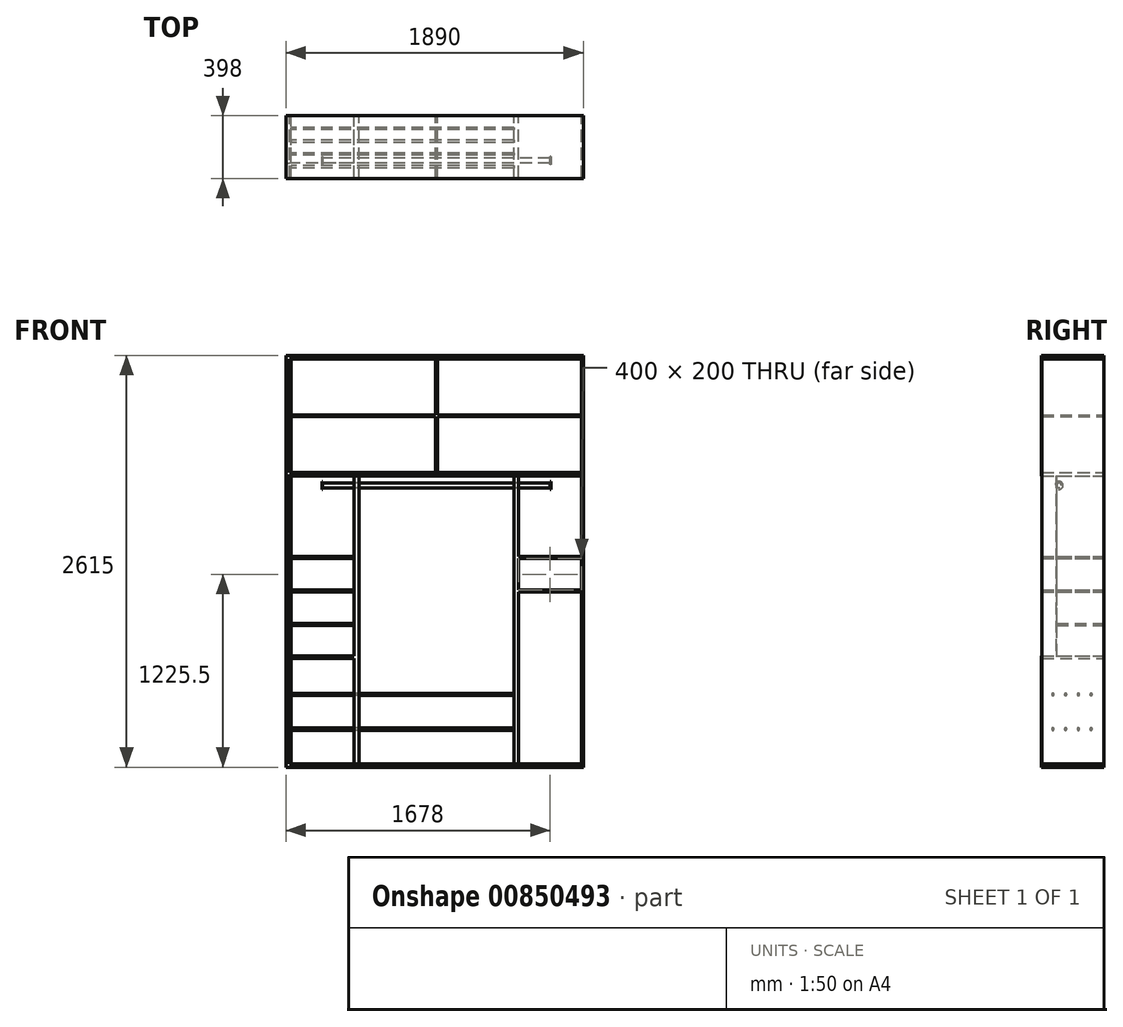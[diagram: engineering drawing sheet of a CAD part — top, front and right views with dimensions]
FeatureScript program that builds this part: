
annotation { "Feature Type Name" : "Feature", "Feature Type Description" : "" }
export const myFeature = defineFeature(function(context is Context, id is Id, definition is map)
    precondition{}
    {
        {
            var Q0;
            Q0=qCreatedBy(makeId("Front.planeOp"),FACE);
            var sketch = newSketch(context, id + "F0", { "sketchPlane" : qUnion([Q0])});
            skLineSegment(sketch, "E0.bottom", {"start": v(0, 0) * mm, "end": v(-1890, 0) * mm});
            skLineSegment(sketch, "E0.top", {"start": v(0, 2615) * mm, "end": v(-1890, 2615) * mm});
            skLineSegment(sketch, "E0.left", {"start": v(0, 0) * mm, "end": v(0, 2615) * mm});
            skLineSegment(sketch, "E0.right", {"start": v(-1890, 0) * mm, "end": v(-1890, 2615) * mm});
            skLineSegment(sketch, "E1", {"start": v(-1868, 2593) * mm, "end": v(0, 2593) * mm});
            skLineSegment(sketch, "E2", {"start": v(-1868, 2593) * mm, "end": v(-1868, 1872) * mm});
            skLineSegment(sketch, "E3", {"start": v(-1868, 22) * mm, "end": v(0, 22) * mm});
            skLineSegment(sketch, "E4", {"start": v(-1868, 1872) * mm, "end": v(-12, 1872) * mm});
            skLineSegment(sketch, "E5", {"start": v(-1868, 1850) * mm, "end": v(-12, 1850) * mm});
            skLineSegment(sketch, "E6", {"start": v(-1456, 1850) * mm, "end": v(-1456, 22) * mm});
            skLineSegment(sketch, "E7", {"start": v(-1426, 1850) * mm, "end": v(-1426, 22) * mm});
            skLineSegment(sketch, "E8", {"start": v(-412, 1850) * mm, "end": v(-412, 22) * mm});
            skLineSegment(sketch, "E9", {"start": v(-442, 1850) * mm, "end": v(-442, 22) * mm});
            skLineSegment(sketch, "E10", {"start": v(-1856, 2593) * mm, "end": v(-1856, 2238.5) * mm});
            skLineSegment(sketch, "E11", {"start": v(-12, 2593) * mm, "end": v(-12, 2238.5) * mm});
            skLineSegment(sketch, "E12.trimOffspring", {"start": v(-1856, 1850) * mm, "end": v(-1856, 22) * mm});
            skLineSegment(sketch, "E13.trimOffspring", {"start": v(-1868, 1850) * mm, "end": v(-1868, 22) * mm});
            skLineSegment(sketch, "E14", {"start": v(-940, 2593) * mm, "end": v(-940, 2238.5) * mm});
            skLineSegment(sketch, "E15", {"start": v(-928, 2593) * mm, "end": v(-928, 2238.5) * mm});
            skPoint(sketch, "E16", {"position": v(-934, 1872) * mm});
            skLineSegment(sketch, "E17", {"start": v(-1856, 2238.5) * mm, "end": v(-940, 2238.5) * mm});
            skLineSegment(sketch, "E18", {"start": v(-1856, 2226.5) * mm, "end": v(-940, 2226.5) * mm});
            skLineSegment(sketch, "E19.trimOffspring", {"start": v(-1856, 2226.5) * mm, "end": v(-1856, 1872) * mm});
            skLineSegment(sketch, "E20.trimOffspring", {"start": v(-928, 2226.5) * mm, "end": v(-928, 1872) * mm});
            skLineSegment(sketch, "E21.trimOffspring", {"start": v(-940, 2226.5) * mm, "end": v(-940, 1872) * mm});
            skLineSegment(sketch, "E22.trimOffspring", {"start": v(-928, 2238.5) * mm, "end": v(-12, 2238.5) * mm});
            skLineSegment(sketch, "E23.trimOffspring", {"start": v(-928, 2226.5) * mm, "end": v(-12, 2226.5) * mm});
            skLineSegment(sketch, "E24.trimOffspring", {"start": v(-12, 2226.5) * mm, "end": v(-12, 22) * mm});
            skSolve(sketch);
        }
        {
            var Q0;
            {var subQ25=sQuery(id+"F0.wireOp",EDGE,"E0.bottom");Q0=makeQuery(id+"F0.imprint","IMPRINT",FACE,{"disambiguationData":[TD([[makeQuery(id+"F0.imprint","IMPRINT",EDGE,{"derivedFrom":subQ25}),-1.0]])]});}
            extrude(context, id + "F1", {"entities" : qUnion([Q0]), "depth" : 398 * mm, "offsetDistance" : 25 * mm});
        }
        {
            var Q0;
            {var subQ0=sQuery(id+"F0.wireOp",EDGE,"E6");Q0=makeQuery(id+"F0.imprint","IMPRINT",FACE,{"disambiguationData":[TD([[makeQuery(id+"F0.imprint","IMPRINT",EDGE,{"derivedFrom":subQ0}),1.0]])]});}
            var Q1;
            {var subQ0=sQuery(id+"F0.wireOp",EDGE,"E8");Q1=makeQuery(id+"F0.imprint","IMPRINT",FACE,{"disambiguationData":[TD([[makeQuery(id+"F0.imprint","IMPRINT",EDGE,{"derivedFrom":subQ0}),-1.0]])]});}
            var Q2;
            {var subQ1=sQuery(id+"F0.wireOp",EDGE,"E2");Q2=makeQuery(id+"F0.imprint","IMPRINT",FACE,{"disambiguationData":[TD([[makeQuery(id+"F0.imprint","IMPRINT",EDGE,{"derivedFrom":subQ1}),1.0]])]});}
            var Q3;
            {var subQ2=sQuery(id+"F0.wireOp",EDGE,"E12.trimOffspring");Q3=makeQuery(id+"F0.imprint","IMPRINT",FACE,{"disambiguationData":[TD([[makeQuery(id+"F0.imprint","IMPRINT",EDGE,{"derivedFrom":subQ2}),-1.0]])]});}
            var Q4;
            Q4=makeQuery(id+"F1.opExtrude","CAP_FACE",FACE,{"disambiguationData":[OSD([sQuery(id+"F0.wireOp",EDGE,"E0.bottom"),sQuery(id+"F0.wireOp",EDGE,"E0.top"),sQuery(id+"F0.wireOp",EDGE,"E0.left"),sQuery(id+"F0.wireOp",EDGE,"E0.right"),sQuery(id+"F0.wireOp",EDGE,"E1"),sQuery(id+"F0.wireOp",EDGE,"E2"),sQuery(id+"F0.wireOp",EDGE,"E3"),sQuery(id+"F0.wireOp",EDGE,"E4"),sQuery(id+"F0.wireOp",EDGE,"E5"),sQuery(id+"F0.wireOp",EDGE,"E13.trimOffspring"),sQuery(id+"F0.wireOp",EDGE,"E24.trimOffspring")])],"isStart":false});
            extrude(context, id + "F2", {"entities" : qUnion([Q0, Q1, Q2, Q3]), "endBound" : BoundingType.UP_TO_SURFACE, "depth" : 25 * mm, "endBoundEntityFace" : qUnion([Q4]), "hasOffset" : true, "offsetDistance" : 5 * mm});
        }
        {
            var Q0;
            Q0=makeQuery(id+"F2.opExtrude","SWEPT_FACE",FACE,{"disambiguationData":[OSD([sQuery(id+"F0.wireOp",EDGE,"E12.trimOffspring")])]});
            var sketch = newSketch(context, id + "F3", { "sketchPlane" : qUnion([Q0])});
            skCircle(sketch, "E25", {"center": v(-324.5, 242) * mm, "radius": 7.5 * mm});
            skCircle(sketch, "E26.0.1.0", {"center": v(-324.5, 462) * mm, "radius": 7.5 * mm});
            skCircle(sketch, "E26.1.0.0", {"center": v(-243.5, 242) * mm, "radius": 7.5 * mm});
            skCircle(sketch, "E26.1.1.0", {"center": v(-243.5, 462) * mm, "radius": 7.5 * mm});
            skCircle(sketch, "E26.2.0.0", {"center": v(-162.5, 242) * mm, "radius": 7.5 * mm});
            skCircle(sketch, "E26.2.1.0", {"center": v(-162.5, 462) * mm, "radius": 7.5 * mm});
            skCircle(sketch, "E26.3.0.0", {"center": v(-81.5, 242) * mm, "radius": 7.5 * mm});
            skCircle(sketch, "E26.3.1.0", {"center": v(-81.5, 462) * mm, "radius": 7.5 * mm});
            skLineSegment(sketch, "E26.direction1", {"start": v(-324.5, 242) * mm, "end": v(-243.5, 242) * mm, "construction": true});
            skLineSegment(sketch, "E26.direction2", {"start": v(-324.5, 242) * mm, "end": v(-324.5, 462) * mm, "construction": true});
            skSolve(sketch);
        }
        {
            var Q0;
            Q0=qSketchRegion(id+"F3",true);
            var Q1;
            Q1=makeQuery(id+"F2.opExtrude","SWEPT_FACE",FACE,{"disambiguationData":[OSD([sQuery(id+"F0.wireOp",EDGE,"E9")])]});
            extrude(context, id + "F4", {"entities" : qUnion([Q0]), "endBound" : BoundingType.UP_TO_SURFACE, "depth" : 25 * mm, "endBoundEntityFace" : qUnion([Q1]), "offsetDistance" : 25 * mm});
        }
        {
            var Q0;
            Q0=qCreatedBy(makeId("Front.planeOp"),FACE);
            var sketch = newSketch(context, id + "F5", { "sketchPlane" : qUnion([Q0])});
            skLineSegment(sketch, "E27.bottom", {"start": v(-1856, 701.5) * mm, "end": v(-1456, 701.5) * mm});
            skLineSegment(sketch, "E27.top", {"start": v(-1856, 689.5) * mm, "end": v(-1456, 689.5) * mm});
            skLineSegment(sketch, "E27.left", {"start": v(-1856, 701.5) * mm, "end": v(-1856, 689.5) * mm});
            skLineSegment(sketch, "E27.right", {"start": v(-1456, 701.5) * mm, "end": v(-1456, 689.5) * mm});
            skLineSegment(sketch, "E28", {"start": v(-1856, 469.5) * mm, "end": v(-442, 469.5) * mm, "construction": true});
            skLineSegment(sketch, "E29.0.1.0", {"start": v(-1856, 913.5) * mm, "end": v(-1456, 913.5) * mm});
            skLineSegment(sketch, "E29.0.1.1", {"start": v(-1856, 901.5) * mm, "end": v(-1456, 901.5) * mm});
            skLineSegment(sketch, "E29.0.1.2", {"start": v(-1856, 913.5) * mm, "end": v(-1856, 901.5) * mm});
            skLineSegment(sketch, "E29.0.1.3", {"start": v(-1456, 913.5) * mm, "end": v(-1456, 901.5) * mm});
            skLineSegment(sketch, "E29.0.2.0", {"start": v(-1856, 1125.5) * mm, "end": v(-1456, 1125.5) * mm});
            skLineSegment(sketch, "E29.0.2.1", {"start": v(-1856, 1113.5) * mm, "end": v(-1456, 1113.5) * mm});
            skLineSegment(sketch, "E29.0.2.2", {"start": v(-1856, 1125.5) * mm, "end": v(-1856, 1113.5) * mm});
            skLineSegment(sketch, "E29.0.2.3", {"start": v(-1456, 1125.5) * mm, "end": v(-1456, 1113.5) * mm});
            skLineSegment(sketch, "E29.0.3.0", {"start": v(-1856, 1337.5) * mm, "end": v(-1456, 1337.5) * mm});
            skLineSegment(sketch, "E29.0.3.1", {"start": v(-1856, 1325.5) * mm, "end": v(-1456, 1325.5) * mm});
            skLineSegment(sketch, "E29.0.3.2", {"start": v(-1856, 1337.5) * mm, "end": v(-1856, 1325.5) * mm});
            skLineSegment(sketch, "E29.0.3.3", {"start": v(-1456, 1337.5) * mm, "end": v(-1456, 1325.5) * mm});
            skLineSegment(sketch, "E29.direction1", {"start": v(-1856, 701.5) * mm, "end": v(-1831, 701.5) * mm, "construction": true});
            skLineSegment(sketch, "E29.direction2", {"start": v(-1856, 701.5) * mm, "end": v(-1856, 913.5) * mm, "construction": true});
            skLineSegment(sketch, "E30.bottom", {"start": v(-412, 1337.5) * mm, "end": v(-12, 1337.5) * mm});
            skLineSegment(sketch, "E30.top", {"start": v(-412, 1325.5) * mm, "end": v(-12, 1325.5) * mm});
            skLineSegment(sketch, "E30.left", {"start": v(-412, 1337.5) * mm, "end": v(-412, 1325.5) * mm});
            skLineSegment(sketch, "E30.right", {"start": v(-12, 1337.5) * mm, "end": v(-12, 1325.5) * mm});
            skLineSegment(sketch, "E31.bottom", {"start": v(-412, 1125.5) * mm, "end": v(-12, 1125.5) * mm});
            skLineSegment(sketch, "E31.top", {"start": v(-412, 1113.5) * mm, "end": v(-12, 1113.5) * mm});
            skLineSegment(sketch, "E31.left", {"start": v(-412, 1125.5) * mm, "end": v(-412, 1113.5) * mm});
            skLineSegment(sketch, "E31.right", {"start": v(-12, 1125.5) * mm, "end": v(-12, 1113.5) * mm});
            skSolve(sketch);
        }
        {
            var Q0;
            Q0=makeQuery(id+"F5.imprint","IMPRINT",FACE,{"disambiguationData":[TD([[makeQuery(id+"F5.imprint","IMPRINT",EDGE,{"derivedFrom":sQuery(id+"F5.wireOp",EDGE,"E29.0.3.0")}),-1.0]])]});
            var Q1;
            Q1=makeQuery(id+"F5.imprint","IMPRINT",FACE,{"disambiguationData":[TD([[makeQuery(id+"F5.imprint","IMPRINT",EDGE,{"derivedFrom":sQuery(id+"F5.wireOp",EDGE,"E29.0.2.0")}),-1.0]])]});
            var Q2;
            Q2=makeQuery(id+"F5.imprint","IMPRINT",FACE,{"disambiguationData":[TD([[makeQuery(id+"F5.imprint","IMPRINT",EDGE,{"derivedFrom":sQuery(id+"F5.wireOp",EDGE,"E29.0.1.0")}),-1.0]])]});
            var Q3;
            Q3=makeQuery(id+"F5.imprint","IMPRINT",FACE,{"disambiguationData":[TD([[makeQuery(id+"F5.imprint","IMPRINT",EDGE,{"derivedFrom":sQuery(id+"F5.wireOp",EDGE,"E27.bottom")}),-1.0]])]});
            var Q4;
            Q4=makeQuery(id+"F5.imprint","IMPRINT",FACE,{"disambiguationData":[TD([[makeQuery(id+"F5.imprint","IMPRINT",EDGE,{"derivedFrom":sQuery(id+"F5.wireOp",EDGE,"E30.bottom")}),-1.0]])]});
            var Q5;
            Q5=makeQuery(id+"F5.imprint","IMPRINT",FACE,{"disambiguationData":[TD([[makeQuery(id+"F5.imprint","IMPRINT",EDGE,{"derivedFrom":sQuery(id+"F5.wireOp",EDGE,"E31.bottom")}),-1.0]])]});
            var Q6;
            Q6=makeQuery(id+"F2.opExtrude","CAP_FACE",FACE,{"disambiguationData":[OSD([sQuery(id+"F0.wireOp",EDGE,"E3"),sQuery(id+"F0.wireOp",EDGE,"E5"),sQuery(id+"F0.wireOp",EDGE,"E6"),sQuery(id+"F0.wireOp",EDGE,"E7")])],"isStart":false});
            extrude(context, id + "F6", {"entities" : qUnion([Q0, Q1, Q2, Q3, Q4, Q5]), "operationType" : NewBodyOperationType.ADD, "endBound" : BoundingType.UP_TO_SURFACE, "depth" : 25 * mm, "endBoundEntityFace" : qUnion([Q6]), "offsetDistance" : 25 * mm});
        }
        {
            var Q0;
            Q0=makeQuery(id+"F1.opExtrude","SWEPT_FACE",FACE,{"disambiguationData":[OSD([sQuery(id+"F0.wireOp",EDGE,"E0.right")])]});
            var sketch = newSketch(context, id + "F7", { "sketchPlane" : qUnion([Q0])});
            skLineSegment(sketch, "E32.0", {"start": v(976.94, 1850) * mm, "end": v(300, 1850) * mm});
            skLineSegment(sketch, "E33.0", {"start": v(964.39, 701.5) * mm, "end": v(300, 701.5) * mm});
            skPoint(sketch, "E34.orphan", {"position": v(393, 701.5) * mm});
            skPoint(sketch, "E35.orphan", {"position": v(393, 1850) * mm});
            skLineSegment(sketch, "E36", {"start": v(300, 1850) * mm, "end": v(300, 701.5) * mm});
            skLineSegment(sketch, "E37", {"start": v(976.94, 1850) * mm, "end": v(964.39, 701.5) * mm});
            skSolve(sketch);
        }
        {
            var Q0;
            Q0=qSketchRegion(id+"F7",true);
            var Q1;
            {var subQ13=sQuery(id+"F0.wireOp",EDGE,"E6");var subQ16=sQuery(id+"F5.wireOp",EDGE,"E29.0.3.0");Q1=makeQuery(id+"F6.boolean.opBoolean","SPLIT",FACE,{"disambiguationData":[TD([makeQuery(id+"F6.opExtrude","SWEPT_FACE",FACE,{"disambiguationData":[OSD([subQ16])]})])],"derivedFrom":makeQuery(id+"F2.opExtrude","SWEPT_FACE",FACE,{"disambiguationData":[OSD([subQ13])]})});}
            extrude(context, id + "F8", {"entities" : qUnion([Q0]), "operationType" : NewBodyOperationType.REMOVE, "endBound" : BoundingType.UP_TO_SURFACE, "oppositeDirection" : true, "depth" : 25 * mm, "endBoundEntityFace" : qUnion([Q1]), "offsetDistance" : 25 * mm});
        }
        {
            var Q0;
            Q0=makeQuery(id+"F8.boolean.opBoolean","COPY",FACE,{"disambiguationData":[TD([makeQuery(id+"F1.opExtrude","SWEPT_FACE",FACE,{"disambiguationData":[OSD([sQuery(id+"F0.wireOp",EDGE,"E0.right")])]})])],"derivedFrom":makeQuery(id+"F8.opExtrude","SWEPT_FACE",FACE,{"disambiguationData":[OSD([sQuery(id+"F7.wireOp",EDGE,"E36")])]})});
            extrude(context, id + "F9", {"entities" : qUnion([Q0]), "operationType" : NewBodyOperationType.ADD, "depth" : 5 * mm, "offsetDistance" : 25 * mm});
        }
        {
            var Q0;
            {var subQ1=sQuery(id+"F0.wireOp",EDGE,"E0.right");Q0=makeQuery(id+"F8.boolean.opBoolean","COPY",FACE,{"disambiguationData":[TD([makeQuery(id+"F1.opExtrude","SWEPT_FACE",FACE,{"disambiguationData":[OSD([subQ1])]})])],"derivedFrom":makeQuery(id+"F8.opExtrude","SWEPT_FACE",FACE,{"disambiguationData":[OSD([sQuery(id+"F7.wireOp",EDGE,"E33.0")])]})});}
            extrude(context, id + "F10", {"entities" : qUnion([Q0]), "operationType" : NewBodyOperationType.ADD, "depth" : 5 * mm, "offsetDistance" : 25 * mm});
        }
        {
            var Q0;
            Q0=makeQuery(id+"F2.opExtrude","SWEPT_FACE",FACE,{"disambiguationData":[OSD([sQuery(id+"F0.wireOp",EDGE,"E7")])]});
            var sketch = newSketch(context, id + "F11", { "sketchPlane" : qUnion([Q0])});
            skCircle(sketch, "E38", {"center": v(-285, 1790) * mm, "radius": 15 * mm});
            skLineSegment(sketch, "E39.0", {"start": v(-393, 22) * mm, "end": v(0, 22) * mm, "construction": true});
            skSolve(sketch);
        }
        {
            var Q0;
            Q0=qSketchRegion(id+"F11",true);
            var Q1;
            Q1=makeQuery(id+"F2.opExtrude","SWEPT_FACE",FACE,{"disambiguationData":[OSD([sQuery(id+"F0.wireOp",EDGE,"E8")])]});
            var Q2;
            {var subQ3=sQuery(id+"F5.wireOp",EDGE,"E29.0.2.0");var subQ8=sQuery(id+"F5.wireOp",EDGE,"E29.0.3.0");var subQ13=sQuery(id+"F5.wireOp",EDGE,"E29.0.1.0");var subQ17=sQuery(id+"F0.wireOp",EDGE,"E6");var subQ25=sQuery(id+"F5.wireOp",EDGE,"E27.bottom");var subQ30=makeQuery(id+"F2.opExtrude","SWEPT_FACE",FACE,{"disambiguationData":[OSD([subQ17])]});Q2=makeQuery(id+"F8.boolean.opBoolean","MERGE",FACE,{"derivedFrom":[makeQuery(id+"F6.boolean.opBoolean","SPLIT",FACE,{"disambiguationData":[TD([makeQuery(id+"F6.opExtrude","SWEPT_FACE",FACE,{"disambiguationData":[OSD([subQ8])]})])],"derivedFrom":subQ30}),makeQuery(id+"F6.boolean.opBoolean","SPLIT",FACE,{"disambiguationData":[TD([makeQuery(id+"F6.opExtrude","SWEPT_FACE",FACE,{"disambiguationData":[OSD([subQ25])]})])],"derivedFrom":subQ30}),makeQuery(id+"F6.boolean.opBoolean","SPLIT",FACE,{"disambiguationData":[TD([makeQuery(id+"F6.opExtrude","SWEPT_FACE",FACE,{"disambiguationData":[OSD([subQ13])]})])],"derivedFrom":subQ30}),makeQuery(id+"F6.boolean.opBoolean","SPLIT",FACE,{"disambiguationData":[TD([makeQuery(id+"F6.opExtrude","SWEPT_FACE",FACE,{"disambiguationData":[OSD([subQ3])]})])],"derivedFrom":subQ30})],"fromTools":[makeQuery(id+"F8.opExtrude","CAP_FACE",FACE,{"disambiguationData":[OSD([sQuery(id+"F7.wireOp",EDGE,"E32.0"),sQuery(id+"F7.wireOp",EDGE,"E33.0"),sQuery(id+"F7.wireOp",EDGE,"E36"),sQuery(id+"F7.wireOp",EDGE,"E37")])],"isStart":false})]});}
            extrude(context, id + "F12", {"entities" : qUnion([Q0]), "endBound" : BoundingType.UP_TO_SURFACE, "depth" : 25 * mm, "endBoundEntityFace" : qUnion([Q1]), "hasOffset" : true, "offsetDistance" : 200 * mm, "offsetOppositeDirection" : true, "hasSecondDirection" : true, "secondDirectionBound" : SecondDirectionBoundingType.UP_TO_SURFACE, "secondDirectionOppositeDirection" : true, "secondDirectionDepth" : 25 * mm, "secondDirectionBoundEntityFace" : qUnion([Q2]), "hasSecondDirectionOffset" : true, "secondDirectionOffsetDistance" : 200 * mm, "secondDirectionOffsetOppositeDirection" : true});
        }
        {
            var Q0;
            Q0=makeQuery(id+"F12.opExtrude","CAP_FACE",FACE,{"disambiguationData":[OSD([sQuery(id+"F11.wireOp",EDGE,"E38")])],"isStart":true});
            var sketch = newSketch(context, id + "F13", { "sketchPlane" : qUnion([Q0])});
            skCircle(sketch, "E40.0", {"center": v(285, 1790) * mm, "radius": 25 * mm});
            skSolve(sketch);
        }
        {
            var Q0;
            Q0=makeQuery(id+"F13.imprint","IMPRINT",FACE,{"disambiguationData":[TD([[makeQuery(id+"F13.imprint","IMPRINT",EDGE,{"derivedFrom":makeQuery(id+"F12.opExtrude","CAP_EDGE",EDGE,{"disambiguationData":[OSD([sQuery(id+"F11.wireOp",EDGE,"E38")])],"isStart":true})}),-1.0]])]});
            var Q1;
            Q1=makeQuery(id+"F13.imprint","IMPRINT",FACE,{"disambiguationData":[TD([[makeQuery(id+"F13.imprint","IMPRINT",EDGE,{"derivedFrom":sQuery(id+"F13.wireOp",EDGE,"E40.0")}),1.0]])]});
            var Q2;
            Q2=sQuery(id+"F13.wireOp",EDGE,"E40.0");
            extrude(context, id + "F14", {"entities" : qUnion([Q0, Q1]), "surfaceEntities" : qUnion([Q2]), "depth" : 5 * mm, "offsetDistance" : 25 * mm});
        }
        {
            var Q0;
            Q0=makeQuery(id+"F12.opExtrude","CAP_FACE",FACE,{"disambiguationData":[OSD([sQuery(id+"F11.wireOp",EDGE,"E38")])],"isStart":false});
            var sketch = newSketch(context, id + "F15", { "sketchPlane" : qUnion([Q0])});
            skCircle(sketch, "E41.0", {"center": v(-285, 1790) * mm, "radius": 25 * mm});
            skSolve(sketch);
        }
        {
            var Q0;
            Q0=makeQuery(id+"F15.imprint","IMPRINT",FACE,{"disambiguationData":[TD([[makeQuery(id+"F15.imprint","IMPRINT",EDGE,{"derivedFrom":makeQuery(id+"F12.opExtrude","CAP_EDGE",EDGE,{"disambiguationData":[OSD([sQuery(id+"F11.wireOp",EDGE,"E38")])],"isStart":false})}),1.0]])]});
            var Q1;
            Q1=makeQuery(id+"F15.imprint","IMPRINT",FACE,{"disambiguationData":[TD([[makeQuery(id+"F15.imprint","IMPRINT",EDGE,{"derivedFrom":sQuery(id+"F15.wireOp",EDGE,"E41.0")}),1.0]])]});
            extrude(context, id + "F16", {"entities" : qUnion([Q0, Q1]), "depth" : 5 * mm, "offsetDistance" : 25 * mm});
        }
    });
